FCSTD DOCUMENT  (FreeCAD 0.16R6712 (Git))
Label: Mini2
License: All rights reserved
LicenseURL: http://en.wikipedia.org/wiki/All_rights_reserved
objects: Part::Box×49, Part::Feature×35, Part::Cylinder×22, Part::MultiFuse×11, Part::Fillet×8, Part::Cut×5, App::DocumentObjectGroup×3, App::VRMLObject×1
note: 130 computed .brp shape members not serialized (recipe doc carries the construction recipe); baked Part::Feature solids carry a one-line shape summary decoded from their .brp

FEATURE [Part::Feature] LCD2X16_MAIN_PART_162  label="HD44780_LCD_2x16"
  Placement = pos=(84.45,6.7,8.8) rot=(0,1,0;3.14159rad)
  shape: bbox 80.5 x 36 x 11.4 mm, 416 faces (baked)
FEATURE [Part::Feature] Part__Feature010  label="Pin_Strip"
  Placement = pos=(76.45,40.225,8.87) rot=(0,0,1;3.14159rad)
  shape: bbox 40.64 x 2.54 x 10.34 mm, 388 faces (baked)
FEATURE [Part::Feature] ISO4032_PART_002  label="Nut_001"
  Placement = pos=(81.775,40.1,8.84) rot=(0,0,1;0rad)
  shape: bbox 6.351 x 6.351 x 3.344 mm, 47 faces (baked)
FEATURE [Part::Box] Box  label="Cube033"
  Height = 4
  Length = 94
  Placement = pos=(-3,-3,0) rot=(0,0,1;0rad)
  Width = 56
FEATURE [Part::Cylinder] Cylinder004  label="Hole001"
  Angle = 360
  Height = 13.4
  Placement = pos=(3.5,3.5,0) rot=(0,0,1;0rad)
  Radius = 1.55
FEATURE [Part::Cylinder] Cylinder005  label="Hole002"
  Angle = 360
  Height = 13.4
  Placement = pos=(3.5,46.5,0) rot=(0,0,1;0rad)
  Radius = 1.55
FEATURE [Part::Cylinder] Cylinder006  label="Hole003"
  Angle = 360
  Height = 13.4
  Placement = pos=(84.5,46.5,0) rot=(0,0,1;0rad)
  Radius = 1.55
FEATURE [Part::Cylinder] Cylinder007  label="Hole004"
  Angle = 360
  Height = 13.4
  Placement = pos=(84.5,3.5,0) rot=(0,0,1;0rad)
  Radius = 1.55
FEATURE [Part::Box] Box001  label="Cube"
  Height = 8.8
  Length = 9.5
  Placement = pos=(-3,-3,3) rot=(0,0,1;0rad)
  Width = 9.5
FEATURE [Part::Fillet] Fillet  label="Fillet010003"
  Base = -> Box001
  Edges = 1 edges r=3: [Edge7]
FEATURE [Part::Box] Box002  label="Cube001"
  Height = 8.8
  Length = 9.5
  Placement = pos=(-3,43.5,3) rot=(0,0,1;0rad)
  Width = 9.5
FEATURE [Part::Fillet] Fillet001  label="Fillet010004"
  Base = -> Box002
  Edges = 1 edges r=3: [Edge5]
FEATURE [Part::Box] Box003  label="Cube002"
  Height = 8.8
  Length = 9.5
  Placement = pos=(81.5,43.5,3) rot=(0,0,1;0rad)
  Width = 9.5
FEATURE [Part::Fillet] Fillet002  label="Fillet010005"
  Base = -> Box003
  Edges = 1 edges r=3: [Edge1]
FEATURE [Part::Box] Box004  label="Cube003"
  Height = 8.8
  Length = 9.5
  Placement = pos=(81.5,-3,3) rot=(0,0,1;0rad)
  Width = 9.5
FEATURE [Part::Fillet] Fillet003  label="Fillet010006"
  Base = -> Box004
  Edges = 1 edges r=3: [Edge3]
FEATURE [Part::MultiFuse] Fusion
  Shapes = -> [Box,Fillet,Fillet001,Fillet002,Fillet003]
FEATURE [Part::MultiFuse] Fusion001
  Shapes = -> [Cylinder004,Cylinder006,Cylinder007,Cylinder005]
FEATURE [Part::Cut] Cut
  Base = -> Fusion
  Tool = -> Fusion001
FEATURE [Part::Cylinder] Cylinder  label="Cylinder001"
  Angle = 360
  Height = 1.5
  Placement = pos=(12.72,-0.5,15.6) rot=(1,0,0;1.5708rad)
  Radius = 2.1
FEATURE [Part::Cylinder] Cylinder008  label="Cylinder002"
  Angle = 360
  Height = 1.5
  Placement = pos=(21.72,-0.5,15.6) rot=(1,0,0;1.5708rad)
  Radius = 2.1
FEATURE [Part::Cylinder] Cylinder009  label="Cylinder003"
  Angle = 360
  Height = 1.5
  Placement = pos=(30.72,-0.5,15.6) rot=(1,0,0;1.5708rad)
  Radius = 2.1
FEATURE [Part::Cylinder] Cylinder010  label="Cylinder004"
  Angle = 360
  Height = 1.5
  Placement = pos=(39.72,-0.5,15.6) rot=(1,0,0;1.5708rad)
  Radius = 2.1
FEATURE [Part::Cylinder] Cylinder011  label="Cylinder005"
  Angle = 360
  Height = 1.5
  Placement = pos=(48.72,-0.5,15.6) rot=(1,0,0;1.5708rad)
  Radius = 2.1
FEATURE [Part::Cylinder] Cylinder012  label="Cylinder006"
  Angle = 360
  Height = 1.5
  Placement = pos=(57.72,-0.5,15.6) rot=(1,0,0;1.5708rad)
  Radius = 2.1
FEATURE [Part::Cylinder] Cylinder013  label="Cylinder007"
  Angle = 360
  Height = 1.5
  Placement = pos=(66.72,-0.5,15.6) rot=(1,0,0;1.5708rad)
  Radius = 2.1
FEATURE [Part::Cylinder] Cylinder014  label="Cylinder008"
  Angle = 360
  Height = 1.5
  Placement = pos=(75.72,-0.5,15.6) rot=(1,0,0;1.5708rad)
  Radius = 2.1
FEATURE [Part::Box] Box006  label="Cube005"
  Height = 10
  Length = 72
  Placement = pos=(8.22,-2,10.6) rot=(0,0,1;0rad)
  Width = 0.75
FEATURE [Part::Box] Box014  label="Cube012"
  Height = 3
  Length = 2.5
  Placement = pos=(-3,-3,11.8) rot=(0,0,1;0rad)
  Width = 9.5
FEATURE [Part::Box] Box015  label="Cube013"
  Height = 3
  Length = 9.5
  Placement = pos=(81.5,-3,11.8) rot=(0,0,1;0rad)
  Width = 2.5
FEATURE [Part::Box] Box016  label="Cube014"
  Height = 3
  Length = 2.5
  Placement = pos=(-3,43.5,11.8) rot=(0,0,1;0rad)
  Width = 9.5
FEATURE [Part::Box] Box017  label="Cube015"
  Height = 3
  Length = 9.5
  Placement = pos=(-3,50.5,11.8) rot=(0,0,1;0rad)
  Width = 2.5
FEATURE [Part::Box] Box018  label="Cube016"
  Height = 3
  Length = 2.5
  Placement = pos=(88.5,-3,11.8) rot=(0,0,1;0rad)
  Width = 9.5
FEATURE [Part::Box] Box019  label="Cube017"
  Height = 3
  Length = 9.5
  Placement = pos=(-3,-3,11.8) rot=(0,0,1;0rad)
  Width = 2.5
FEATURE [Part::Box] Box020  label="Cube018"
  Height = 3
  Length = 2.5
  Placement = pos=(88.5,43.5,11.8) rot=(0,0,1;0rad)
  Width = 9.5
FEATURE [Part::Box] Box021  label="Cube019"
  Height = 3
  Length = 9.5
  Placement = pos=(81.5,50.5,11.8) rot=(0,0,1;0rad)
  Width = 2.5
FEATURE [Part::Feature] Fusion003005009005  label="Hole013"
  Placement = pos=(84.5,3.5,1.65) rot=(1,0,0;3.14159rad)
  shape: bbox 6 x 6 x 3 mm, 5 faces (baked)
FEATURE [Part::Feature] ISO7092_PART_1  label="Washer_001"
  Placement = pos=(81.775,40.1,11.245) rot=(0,0,1;0rad)
  shape: bbox 6 x 6 x 0.55 mm, 4 faces (baked)
FEATURE [Part::Feature] ISO7092_PART_002  label="Washer_002"
  Placement = pos=(7.1,40.1,11.245) rot=(0,0,1;0rad)
  shape: bbox 6 x 6 x 0.55 mm, 4 faces (baked)
FEATURE [Part::Feature] ISO7092_PART_003  label="Washer_003"
  Placement = pos=(81.775,9.35,11.245) rot=(0,0,1;0rad)
  shape: bbox 6 x 6 x 0.55 mm, 4 faces (baked)
FEATURE [Part::Feature] ISO7092_PART_004  label="Washer_004"
  Placement = pos=(7.1,9.35,11.245) rot=(0,0,1;0rad)
  shape: bbox 6 x 6 x 0.55 mm, 4 faces (baked)
FEATURE [Part::Feature] ISO4032_PART_003  label="Nut_002"
  Placement = pos=(7.1,40.1,8.84) rot=(0,0,1;0rad)
  shape: bbox 6.351 x 6.351 x 3.344 mm, 47 faces (baked)
FEATURE [Part::Feature] ISO4032_PART_004  label="Nut_003"
  Placement = pos=(81.775,9.35,8.84) rot=(0,0,1;0rad)
  shape: bbox 6.351 x 6.351 x 3.344 mm, 47 faces (baked)
FEATURE [Part::Feature] ISO4032_PART_005  label="Nut_004"
  Placement = pos=(7.1,9.35,8.84) rot=(0,0,1;0rad)
  shape: bbox 6.351 x 6.351 x 3.344 mm, 47 faces (baked)
FEATURE [Part::Feature] ISO7048_PART_3  label="Screw_001"
  Placement = pos=(81.775,40.1,7.15) rot=(1,0,0;3.14159rad)
  shape: bbox 5.526 x 5.5 x 12.5 mm, 110 faces (baked)
FEATURE [Part::Feature] ISO4032_PART_006  label="Nut_005"
  Placement = pos=(81.775,40.1,13.45) rot=(0,0,1;0rad)
  shape: bbox 6.351 x 6.351 x 3.344 mm, 47 faces (baked)
FEATURE [Part::Feature] ISO7048_PART_004  label="Screw_002"
  Placement = pos=(7.1,40.1,7.15) rot=(1,0,0;3.14159rad)
  shape: bbox 5.526 x 5.5 x 12.5 mm, 110 faces (baked)
FEATURE [Part::Feature] ISO7048_PART_005  label="Screw_003"
  Placement = pos=(81.775,9.35,7.15) rot=(1,0,0;3.14159rad)
  shape: bbox 5.526 x 5.5 x 12.5 mm, 110 faces (baked)
FEATURE [Part::Feature] ISO7048_PART_006  label="Screw_004"
  Placement = pos=(7.1,9.35,7.15) rot=(1,0,0;3.14159rad)
  shape: bbox 5.526 x 5.5 x 12.5 mm, 110 faces (baked)
FEATURE [Part::Feature] ISO4032_PART_007  label="Nut_006"
  Placement = pos=(7.1,40.1,13.45) rot=(0,0,1;0rad)
  shape: bbox 6.351 x 6.351 x 3.344 mm, 47 faces (baked)
FEATURE [Part::Feature] ISO4032_PART_008  label="Nut_007"
  Placement = pos=(81.775,9.35,13.45) rot=(0,0,1;0rad)
  shape: bbox 6.351 x 6.351 x 3.344 mm, 47 faces (baked)
FEATURE [Part::Feature] ISO4032_PART_009  label="Nut_008"
  Placement = pos=(7.1,9.35,13.45) rot=(0,0,1;0rad)
  shape: bbox 6.351 x 6.351 x 3.344 mm, 47 faces (baked)
FEATURE [Part::Box] Box022  label="Cut_Display"
  Height = 4
  Length = 71.4
  Placement = pos=(8.75,12.5,0) rot=(0,0,1;0rad)
  Width = 24.4
FEATURE [Part::Box] Box023  label="Cube021"
  Height = 10.6
  Length = 75
  Placement = pos=(6.5,-3,0) rot=(0,0,1;0rad)
  Width = 3.5
FEATURE [Part::Box] Box024  label="Cube022"
  Height = 10.6
  Length = 75
  Placement = pos=(6.5,49.5,0) rot=(0,0,1;0rad)
  Width = 3.5
FEATURE [Part::Box] Box025  label="Cube023"
  Height = 10.6
  Length = 3.5
  Placement = pos=(-3,6.5,0) rot=(0,0,1;0rad)
  Width = 37
FEATURE [Part::Box] Box026  label="Cube024"
  Height = 10.6
  Length = 3.5
  Placement = pos=(87.5,6.5,0) rot=(0,0,1;0rad)
  Width = 37
FEATURE [Part::MultiFuse] Fusion003005009006
  Shapes = -> [Box024,Box025,Box026,Box023,Box014,Box015,Box016,Box017,Box018,Box019,Box020,Box021,Cut]
FEATURE [Part::Feature] Fusion003005009007  label="Hole014"
  Placement = pos=(84.5,46.5,1.65) rot=(1,0,0;3.14159rad)
  shape: bbox 6 x 6 x 3 mm, 5 faces (baked)
FEATURE [Part::Feature] Fusion003005009008  label="Hole015"
  Placement = pos=(3.5,3.5,1.65) rot=(1,0,0;3.14159rad)
  shape: bbox 6 x 6 x 3 mm, 5 faces (baked)
FEATURE [Part::Feature] Fusion003005009009  label="Hole016"
  Placement = pos=(3.5,46.5,1.65) rot=(1,0,0;3.14159rad)
  shape: bbox 6 x 6 x 3 mm, 5 faces (baked)
FEATURE [Part::MultiFuse] Fusion003005009010
  Shapes = -> [Fusion003005009005,Fusion003005009007,Fusion003005009009,Fusion003005009008]
FEATURE [Part::Cut] Cut001  label="Cut004"
  Base = -> Fusion003005009006
  Tool = -> Fusion003005009010
FEATURE [Part::MultiFuse] Fusion003005009011
  Shapes = -> [Box006,Cylinder010,Cylinder008,Cylinder011,Cylinder013,Cylinder012,Cylinder014,Cylinder009,Cylinder]
FEATURE [Part::Box] Box027  label="Cube025"
  Height = 5.2
  Length = 78
  Placement = pos=(5,-2,9.6) rot=(0,0,1;0rad)
  Width = 1.5
FEATURE [Part::Box] Box028  label="Cube026"
  Height = 12
  Length = 78
  Placement = pos=(5.22,-2,9.6) rot=(0,0,1;0rad)
  Width = 1.5
FEATURE [Part::Feature] Cut003001  label="LED_D2"
  shape: bbox 3.5 x 3.8 x 15.8 mm, 33 faces (baked)
FEATURE [Part::Feature] Cut003002001  label="LED_D3"
  shape: bbox 3.5 x 3.8 x 15.8 mm, 33 faces (baked)
FEATURE [App::DocumentObjectGroup] Group  label="Components"
  Group = -> [LCD2X16_MAIN_PART_162,Part__Feature010,ISO7092_PART_1,ISO7092_PART_002,ISO7092_PART_003,ISO7092_PART_004,ISO4032_PART_002,ISO4032_PART_003,ISO4032_PART_004,ISO4032_PART_005,ISO7048_PART_3,ISO7048_PART_004,ISO7048_PART_005,ISO7048_PART_006,ISO4032_PART_006,ISO4032_PART_007,ISO4032_PART_008,ISO4032_PART_009,Cut003001,Cut003002001]
FEATURE [Part::Cylinder] Cylinder015  label="Cut_D2"
  Angle = 360
  Height = 4
  Placement = pos=(40.9,45.95,0) rot=(0,0,1;0rad)
  Radius = 1.6
FEATURE [Part::Cylinder] Cylinder016  label="Cut_D3"
  Angle = 360
  Height = 4
  Placement = pos=(77.1,45.95,0) rot=(0,0,1;0rad)
  Radius = 1.6
FEATURE [Part::Box] Box030  label="Cube028"
  Height = 2
  Length = 94
  Placement = pos=(-3,-3,39) rot=(0,0,1;0rad)
  Width = 56
FEATURE [Part::Feature] Part__Feature_solid  label="9V"
  shape: bbox 49 x 45.3 x 22 mm, 743 faces (baked)
FEATURE [Part::MultiFuse] Fusion003005009013
  Shapes = -> [Box030,Part__Feature_solid]
FEATURE [App::VRMLObject] BBMini2
  Placement = pos=(0,0,12.63) rot=(0,0,1;0rad)
FEATURE [Part::Box] Box031  label="Cube029"
  Height = 5.2
  Length = 78
  Placement = pos=(5.22,50.5,9.6) rot=(0,0,1;0rad)
  Width = 1.5
FEATURE [Part::Box] Box032  label="Cube030"
  Height = 5.2
  Length = 1.5
  Placement = pos=(-2,5,9.6) rot=(0,0,1;0rad)
  Width = 40
FEATURE [Part::Box] Box033  label="Cube031"
  Height = 5.2
  Length = 1.5
  Placement = pos=(88.5,5,9.6) rot=(0,0,1;0rad)
  Width = 40
FEATURE [Part::MultiFuse] Fusion003005009014
  Shapes = -> [Box031,Cylinder016,Cylinder015,Box027,Box022,Box032,Box033]
FEATURE [Part::Cut] Cut003002002
  Base = -> Cut001
  Tool = -> Fusion003005009014
FEATURE [Part::Box] Box034  label="Cube032"
  Height = 25.5
  Length = 9.5
  Placement = pos=(-3,-3,13.5) rot=(0,0,1;0rad)
  Width = 9.5
FEATURE [Part::Fillet] Fillet004  label="Fillet010007"
  Base = -> Box034
  Edges = 1 edges r=3: [Edge7]
FEATURE [Part::Box] Box035  label="Cube034"
  Height = 25.5
  Length = 9.5
  Placement = pos=(-3,43.5,13.5) rot=(0,0,1;0rad)
  Width = 9.5
FEATURE [Part::Fillet] Fillet005  label="Fillet010008"
  Base = -> Box035
  Edges = 1 edges r=3: [Edge5]
FEATURE [Part::Box] Box036  label="Cube035"
  Height = 25.5
  Length = 9.5
  Placement = pos=(81.5,43.5,13.5) rot=(0,0,1;0rad)
  Width = 9.5
FEATURE [Part::Fillet] Fillet006  label="Fillet010009"
  Base = -> Box036
  Edges = 1 edges r=3: [Edge1]
FEATURE [Part::Box] Box037  label="Cube036"
  Height = 25.5
  Length = 9.5
  Placement = pos=(81.5,-3,13.5) rot=(0,0,1;0rad)
  Width = 9.5
FEATURE [Part::Fillet] Fillet007  label="Fillet010010"
  Base = -> Box037
  Edges = 1 edges r=3: [Edge3]
FEATURE [Part::MultiFuse] Fusion003005009015
  Shapes = -> [Fusion003005009013,Fillet004,Fillet005,Fillet006,Fillet007]
FEATURE [Part::Box] Box038  label="Cube037"
  Height = 3
  Length = 9.5
  Placement = pos=(81.5,50.5,11.8) rot=(0,0,1;0rad)
  Width = 2.5
FEATURE [Part::Box] Box039  label="Cube038"
  Height = 3
  Length = 2.5
  Placement = pos=(88.5,43.5,11.8) rot=(0,0,1;0rad)
  Width = 9.5
FEATURE [Part::Box] Box040  label="Cube039"
  Height = 3
  Length = 9.5
  Placement = pos=(-3,-3,11.8) rot=(0,0,1;0rad)
  Width = 2.5
FEATURE [Part::Box] Box041  label="Cube040"
  Height = 3
  Length = 2.5
  Placement = pos=(88.5,-3,11.8) rot=(0,0,1;0rad)
  Width = 9.5
FEATURE [Part::Box] Box042  label="Cube041"
  Height = 3
  Length = 9.5
  Placement = pos=(-3,50.5,11.8) rot=(0,0,1;0rad)
  Width = 2.5
FEATURE [Part::Box] Box043  label="Cube042"
  Height = 3
  Length = 2.5
  Placement = pos=(-3,43.5,11.8) rot=(0,0,1;0rad)
  Width = 9.5
FEATURE [Part::Box] Box044  label="Cube043"
  Height = 3
  Length = 9.5
  Placement = pos=(81.5,-3,11.8) rot=(0,0,1;0rad)
  Width = 2.5
FEATURE [Part::Box] Box045  label="Cube044"
  Height = 3
  Length = 2.5
  Placement = pos=(-3,-3,11.8) rot=(0,0,1;0rad)
  Width = 9.5
FEATURE [Part::MultiFuse] Fusion003005009016
  Shapes = -> [Box038,Box043,Box044,Box042,Box041,Box040,Box045,Box039]
FEATURE [Part::Cut] Cut003002003
  Base = -> Fusion003005009015
  Tool = -> Fusion003005009016
FEATURE [Part::Box] Box046  label="Cube045"
  Height = 12
  Length = 75
  Placement = pos=(6.5,49.5,27) rot=(0,0,1;0rad)
  Width = 3.5
FEATURE [Part::Box] Box047  label="Cube046"
  Height = 12
  Length = 3.5
  Placement = pos=(87.5,6.5,27) rot=(0,0,1;0rad)
  Width = 37
FEATURE [Part::Box] Box048  label="Cube047"
  Height = 12
  Length = 3.5
  Placement = pos=(-3,6.5,27) rot=(0,0,1;0rad)
  Width = 37
FEATURE [Part::Box] Box049  label="Cube048"
  Height = 12
  Length = 75
  Placement = pos=(6.5,-3,27) rot=(0,0,1;0rad)
  Width = 3.5
FEATURE [Part::Box] Box050  label="Cube049"
  Height = 13.2
  Length = 78
  Placement = pos=(5.22,50.5,14.8) rot=(0,0,1;0rad)
  Width = 1.5
FEATURE [Part::Box] Box051  label="Cube050"
  Height = 13.2
  Length = 78
  Placement = pos=(5,-2,14.8) rot=(0,0,1;0rad)
  Width = 1.5
FEATURE [Part::Box] Box052  label="Cube051"
  Height = 13.2
  Length = 1.5
  Placement = pos=(-2,5,14.8) rot=(0,0,1;0rad)
  Width = 40
FEATURE [Part::Box] Box053  label="Cube052"
  Height = 13.2
  Length = 1.5
  Placement = pos=(88.5,5,14.8) rot=(0,0,1;0rad)
  Width = 40
FEATURE [Part::Cylinder] Cylinder017  label="Hole017"
  Angle = 360
  Height = 29.5
  Placement = pos=(3.5,3.5,13.5) rot=(0,0,1;0rad)
  Radius = 1.55
FEATURE [Part::Cylinder] Cylinder018  label="Hole018"
  Angle = 360
  Height = 29.5
  Placement = pos=(3.5,46.5,13.5) rot=(0,0,1;0rad)
  Radius = 1.55
FEATURE [Part::Cylinder] Cylinder019  label="Hole019"
  Angle = 360
  Height = 29.5
  Placement = pos=(84.5,46.5,13.5) rot=(0,0,1;0rad)
  Radius = 1.55
FEATURE [Part::Cylinder] Cylinder020  label="Hole020"
  Angle = 360
  Height = 29.5
  Placement = pos=(84.5,3.5,13.5) rot=(0,0,1;0rad)
  Radius = 1.55
FEATURE [Part::Cylinder] Cylinder021  label="Cylinder"
  Angle = 360
  Height = 3.5
  Placement = pos=(3.5,3.5,37.5) rot=(0,0,1;0rad)
  Radius = 3.4
FEATURE [Part::Cylinder] Cylinder022  label="Cylinder009"
  Angle = 360
  Height = 3.5
  Placement = pos=(3.5,46.5,37.5) rot=(0,0,1;0rad)
  Radius = 3.4
FEATURE [Part::Cylinder] Cylinder023  label="Cylinder010"
  Angle = 360
  Height = 3.5
  Placement = pos=(84.5,3.5,37.5) rot=(0,0,1;0rad)
  Radius = 3.4
FEATURE [Part::Cylinder] Cylinder024  label="Cylinder011"
  Angle = 360
  Height = 3.5
  Placement = pos=(84.5,46.5,37.5) rot=(0,0,1;0rad)
  Radius = 3.4
FEATURE [Part::MultiFuse] Fusion003005009018
  Shapes = -> [Box050,Cylinder021,Cylinder023,Cylinder024,Cylinder020,Box052,Box053,Cylinder018,Cylinder022,Cylinder017,Box051,Cylinder019]
FEATURE [Part::Feature] Fillet009003001  label="Case_Bottom"
  shape: bbox 94.49 x 56.49 x 14.8 mm, 112 faces (baked)
FEATURE [Part::Feature] ISO7046_PART_3  label="Case_Screw_001"
  Placement = pos=(3.5,3.5,0) rot=(1,0,0;3.14159rad)
  shape: bbox 5.426 x 5.3 x 40.5 mm, 233 faces (baked)
FEATURE [Part::Box] Box054  label="Cube053"
  Height = 5
  Length = 8
  Placement = pos=(0.5,0.5,34) rot=(0,0,1;0rad)
  Width = 8
FEATURE [Part::Box] Box055  label="Cube054"
  Height = 5
  Length = 8
  Placement = pos=(0.5,41.5,34) rot=(0,0,1;0rad)
  Width = 8
FEATURE [Part::Box] Box056  label="Cube055"
  Height = 5
  Length = 8
  Placement = pos=(79.5,0.5,34) rot=(0,0,1;0rad)
  Width = 8
FEATURE [Part::Box] Box057  label="Cube056"
  Height = 5
  Length = 8
  Placement = pos=(79.5,41.5,34) rot=(0,0,1;0rad)
  Width = 8
FEATURE [Part::MultiFuse] Fusion003005009019
  Shapes = -> [Box054,Box055,Box056,Box057,Cut003002003,Box048,Box046,Box047,Box049]
FEATURE [Part::Cut] Cut003002004
  Base = -> Fusion003005009019
  Tool = -> Fusion003005009018
FEATURE [App::DocumentObjectGroup] Group001  label="Work"
  Group = -> [Cut003002002,Cut003002004]
FEATURE [Part::Feature] ISO7046_PART_004  label="Case_Screw_002"
  Placement = pos=(3.5,46.5,0) rot=(1,0,0;3.14159rad)
  shape: bbox 5.426 x 5.3 x 40.5 mm, 233 faces (baked)
FEATURE [Part::Feature] ISO7046_PART_005  label="Case_Screw_003"
  Placement = pos=(84.5,3.5,0) rot=(1,0,0;3.14159rad)
  shape: bbox 5.426 x 5.3 x 40.5 mm, 233 faces (baked)
FEATURE [Part::Feature] ISO7046_PART_006  label="Case_Screw_004"
  Placement = pos=(84.5,46.5,0) rot=(1,0,0;3.14159rad)
  shape: bbox 5.426 x 5.3 x 40.5 mm, 233 faces (baked)
FEATURE [Part::Feature] ISO4032_PART_1  label="Case_Nut_001"
  Placement = pos=(3.5,3.5,37.5) rot=(0,0,1;0rad)
  shape: bbox 6.351 x 6.351 x 3.344 mm, 47 faces (baked)
FEATURE [Part::Feature] Fillet009003003001  label="Case_Top"
  shape: bbox 94.49 x 56.49 x 27.5 mm, 656 faces (baked)
FEATURE [Part::Feature] ISO4032_PART_010  label="Case_Nut_002"
  Placement = pos=(3.5,46.5,37.5) rot=(0,0,1;0rad)
  shape: bbox 6.351 x 6.351 x 3.344 mm, 47 faces (baked)
FEATURE [Part::Feature] ISO4032_PART_011  label="Case_Nut_003"
  Placement = pos=(84.5,3.5,37.5) rot=(0,0,1;0rad)
  shape: bbox 6.351 x 6.351 x 3.344 mm, 47 faces (baked)
FEATURE [Part::Feature] ISO4032_PART_012  label="Case_Nut_004"
  Placement = pos=(84.5,46.5,37.5) rot=(0,0,1;0rad)
  shape: bbox 6.351 x 6.351 x 3.344 mm, 47 faces (baked)
FEATURE [App::DocumentObjectGroup] Group002  label="Case"
  Group = -> [Fillet009003001,ISO7046_PART_3,ISO7046_PART_004,ISO7046_PART_005,ISO7046_PART_006,Fillet009003003001,ISO4032_PART_1,ISO4032_PART_010,ISO4032_PART_011,ISO4032_PART_012]
